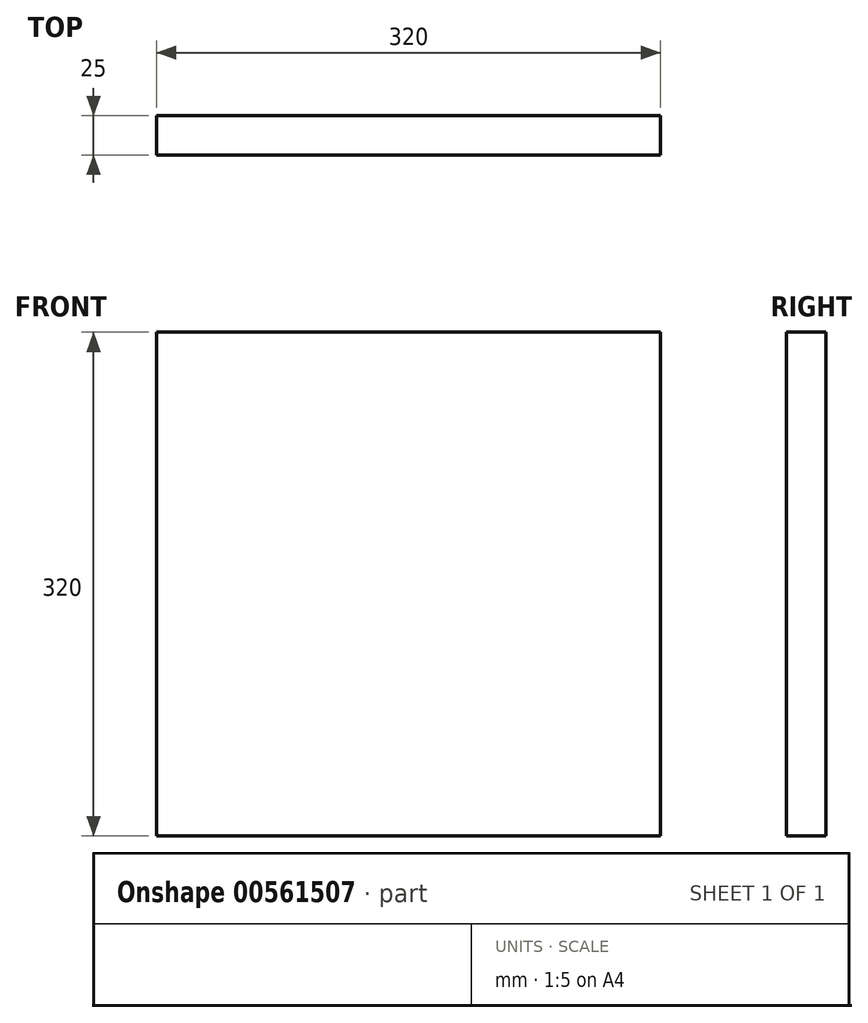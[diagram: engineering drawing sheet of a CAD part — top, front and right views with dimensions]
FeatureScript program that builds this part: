
annotation { "Feature Type Name" : "Feature", "Feature Type Description" : "" }
export const myFeature = defineFeature(function(context is Context, id is Id, definition is map)
    precondition{}
    {
        {
            var Q0;
            Q0=qCreatedBy(makeId("Front.planeOp"),FACE);
            var sketch = newSketch(context, id + "F0", { "sketchPlane" : qUnion([Q0])});
            skLineSegment(sketch, "E0.bottom", {"start": v(0, 0) * mm, "end": v(320, 0) * mm});
            skLineSegment(sketch, "E0.top", {"start": v(0, 320) * mm, "end": v(320, 320) * mm});
            skLineSegment(sketch, "E0.left", {"start": v(0, 0) * mm, "end": v(0, 320) * mm});
            skLineSegment(sketch, "E0.right", {"start": v(320, 0) * mm, "end": v(320, 320) * mm});
            skSolve(sketch);
        }
        {
            var Q0;
            Q0 = qSketchRegion(id + "F0", true);
            extrude(context, id + "F1", {"entities" : qUnion([Q0]), "depth" : 25 * mm, "offsetDistance" : 25 * mm, "symmetric" : true});
        }
    });
